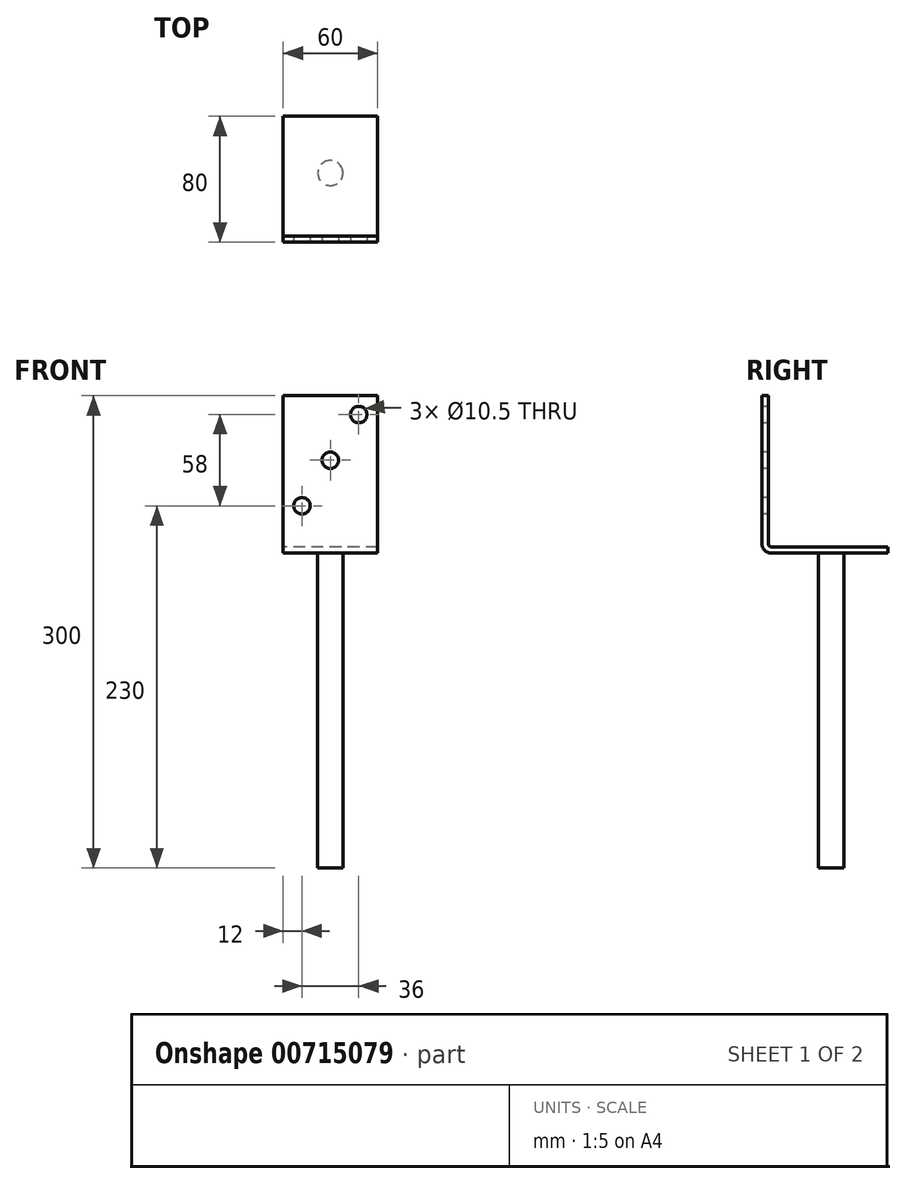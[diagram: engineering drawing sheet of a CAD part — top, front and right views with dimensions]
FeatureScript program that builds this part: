
annotation { "Feature Type Name" : "Feature", "Feature Type Description" : "" }
export const myFeature = defineFeature(function(context is Context, id is Id, definition is map)
    precondition{}
    {
        {
            var Q0;
            Q0=qCreatedBy(makeId("Right.planeOp"),FACE);
            var sketch = newSketch(context, id + "F0", { "sketchPlane" : qUnion([Q0])});
            skLineSegment(sketch, "E0", {"start": v(-40, -50) * mm, "end": v(-40, 46) * mm});
            skLineSegment(sketch, "E1", {"start": v(-40, 46) * mm, "end": v(-44, 46) * mm});
            skLineSegment(sketch, "E2", {"start": v(-44, 46) * mm, "end": v(-44, -54) * mm});
            skLineSegment(sketch, "E3", {"start": v(-44, -54) * mm, "end": v(36, -54) * mm});
            skLineSegment(sketch, "E4", {"start": v(-40, -50) * mm, "end": v(36, -50) * mm});
            skLineSegment(sketch, "E5", {"start": v(36, -50) * mm, "end": v(36, -54) * mm});
            skSolve(sketch);
        }
        {
            var Q0;
            Q0=makeQuery(id+"F0.imprint","IMPRINT",FACE,{"disambiguationData":[TD([[makeQuery(id+"F0.imprint","IMPRINT",EDGE,{"derivedFrom":sQuery(id+"F0.wireOp",EDGE,"a4176c50-ce27-4d29-83f8-b5d18df032a8")}),1.0]])]});
            var Q1;
            Q1=makeQuery(id+"F0.imprint","IMPRINT",FACE,{"disambiguationData":[TD([[makeQuery(id+"F0.imprint","IMPRINT",EDGE,{"derivedFrom":sQuery(id+"F0.wireOp",EDGE,"E0")}),1.0]])]});
            extrude(context, id + "F1", {"entities" : qUnion([Q0, Q1]), "endBound" : BoundingType.SYMMETRIC, "depth" : 60 * mm, "offsetDistance" : 25 * mm});
        }
        {
            var Q0;
            Q0=makeQuery(id+"F1.opExtrude","SWEPT_FACE",FACE,{"disambiguationData":[OSD([sQuery(id+"F0.wireOp",EDGE,"E3")])]});
            var sketch = newSketch(context, id + "F2", { "sketchPlane" : qUnion([Q0])});
            skCircle(sketch, "E6", {"center": v(0, 0) * mm, "radius": 8 * mm});
            skSolve(sketch);
        }
        {
            var Q0;
            Q0=makeQuery(id+"F2.imprint","IMPRINT",FACE,{"disambiguationData":[TD([[makeQuery(id+"F2.imprint","IMPRINT",EDGE,{"derivedFrom":sQuery(id+"F2.wireOp",EDGE,"E6")}),1.0]])]});
            extrude(context, id + "F3", {"entities" : qUnion([Q0]), "operationType" : NewBodyOperationType.ADD, "depth" : 200 * mm, "offsetDistance" : 25 * mm});
        }
        {
            var Q0;
            Q0=makeQuery(id+"F1.opExtrude","SWEPT_FACE",FACE,{"disambiguationData":[OSD([sQuery(id+"F0.wireOp",EDGE,"E2")])]});
            var sketch = newSketch(context, id + "F4", { "sketchPlane" : qUnion([Q0])});
            skLineSegment(sketch, "E7", {"start": v(-18, -24) * mm, "end": v(18, 34) * mm, "construction": true});
            skCircle(sketch, "E8", {"center": v(18, 34) * mm, "radius": 5.25 * mm});
            skCircle(sketch, "E9", {"center": v(0, 5) * mm, "radius": 5.25 * mm});
            skCircle(sketch, "E10", {"center": v(-18, -24) * mm, "radius": 5.25 * mm});
            skSolve(sketch);
        }
        {
            var Q0;
            Q0=makeQuery(id+"F1.opExtrude","SWEPT_EDGE",EDGE,{"disambiguationData":[OSD([sQuery(id+"F0.wireOp",EDGE,"E0"),sQuery(id+"F0.wireOp",EDGE,"E4")])]});
            fillet(context, id + "F5", {"entities" : qUnion([Q0]), "radius" : 2 * mm, "tangentPropagation" : true, "allowEdgeOverflow" : false});
        }
        {
            var Q0;
            Q0=makeQuery(id+"F1.opExtrude","SWEPT_EDGE",EDGE,{"disambiguationData":[OSD([sQuery(id+"F0.wireOp",EDGE,"E2"),sQuery(id+"F0.wireOp",EDGE,"E3")])]});
            fillet(context, id + "F6", {"entities" : qUnion([Q0]), "radius" : 6 * mm, "tangentPropagation" : true, "allowEdgeOverflow" : false});
        }
        {
            var Q0;
            Q0 = qSketchRegion(id + "F4", true);
            extrude(context, id + "F7", {"entities" : qUnion([Q0]), "operationType" : NewBodyOperationType.REMOVE, "oppositeDirection" : true, "depth" : 25 * mm, "offsetDistance" : 25 * mm});
        }
    });
